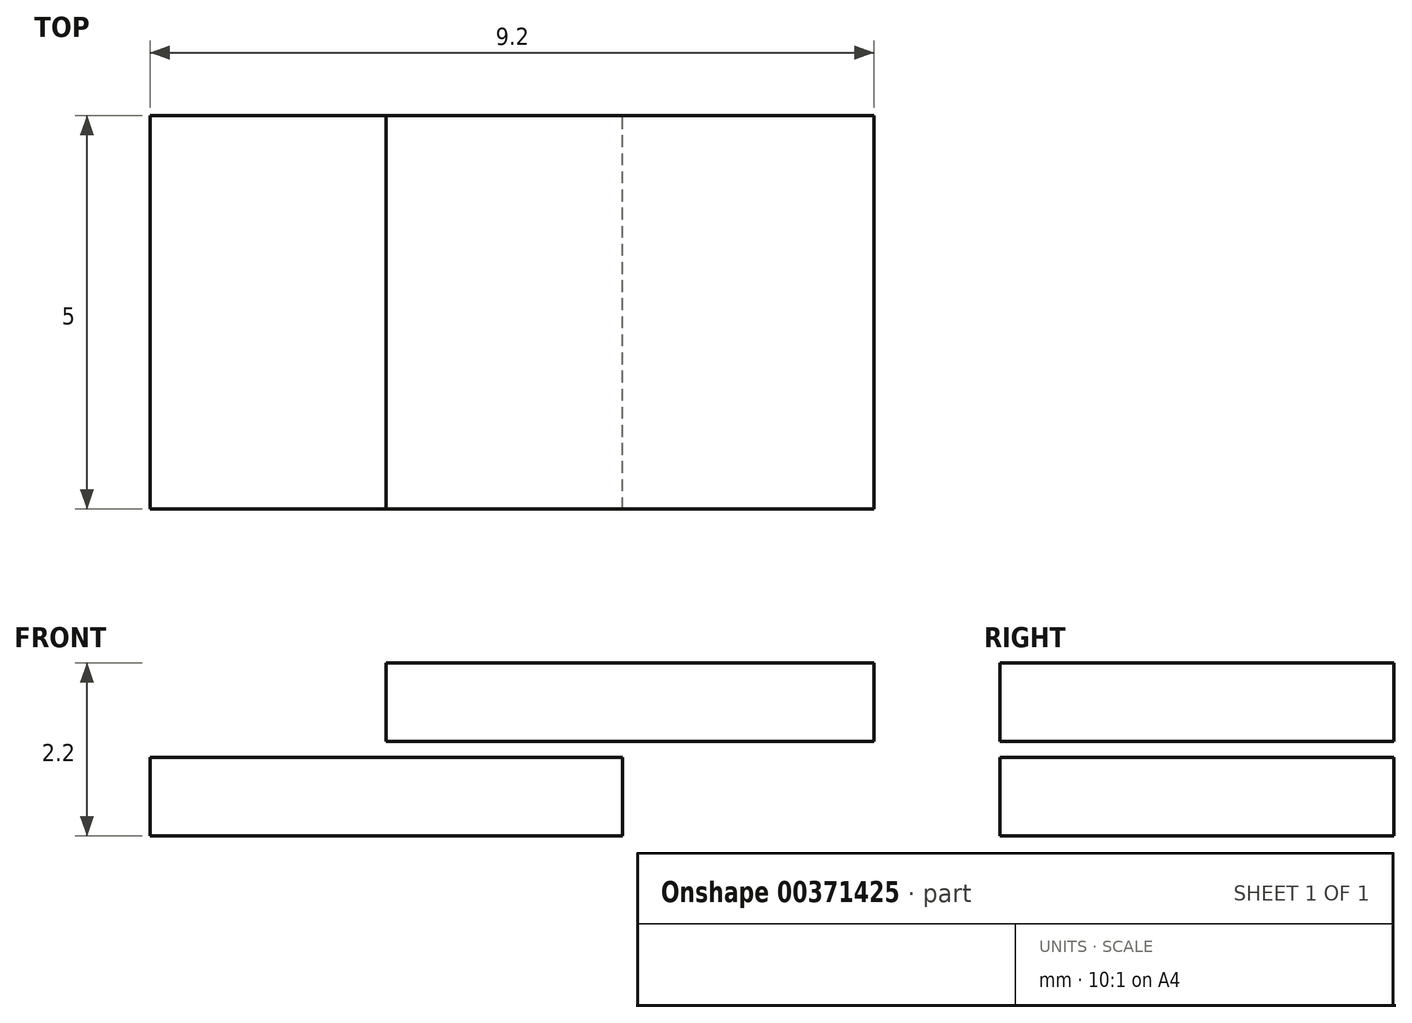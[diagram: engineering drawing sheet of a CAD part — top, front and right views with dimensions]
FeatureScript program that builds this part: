
annotation { "Feature Type Name" : "Feature", "Feature Type Description" : "" }
export const myFeature = defineFeature(function(context is Context, id is Id, definition is map)
    precondition{}
    {
        {
            var Q0;
            Q0=qCreatedBy(makeId("Front.planeOp"),FACE);
            var sketch = newSketch(context, id + "F0", { "sketchPlane" : qUnion([Q0])});
            skLineSegment(sketch, "E0.bottom", {"start": v(0, 0) * mm, "end": v(-6, 0) * mm});
            skLineSegment(sketch, "E0.top", {"start": v(0, 1) * mm, "end": v(-6, 1) * mm});
            skLineSegment(sketch, "E0.left", {"start": v(0, 0) * mm, "end": v(0, 1) * mm});
            skLineSegment(sketch, "E0.right", {"start": v(-6, 0) * mm, "end": v(-6, 1) * mm});
            skLineSegment(sketch, "E1.bottom", {"start": v(-3, 2.2) * mm, "end": v(3.2, 2.2) * mm});
            skLineSegment(sketch, "E1.top", {"start": v(-3, 1.2) * mm, "end": v(3.2, 1.2) * mm});
            skLineSegment(sketch, "E1.left", {"start": v(-3, 2.2) * mm, "end": v(-3, 1.2) * mm});
            skLineSegment(sketch, "E1.right", {"start": v(3.2, 2.2) * mm, "end": v(3.2, 1.2) * mm});
            skLineSegment(sketch, "E2.bottom", {"start": v(3.2, 1.2) * mm, "end": v(0.2, 1.2) * mm});
            skLineSegment(sketch, "E2.top", {"start": v(3.2, 0) * mm, "end": v(0.2, 0) * mm});
            skLineSegment(sketch, "E2.left", {"start": v(3.2, 1.2) * mm, "end": v(3.2, 0) * mm});
            skLineSegment(sketch, "E2.right", {"start": v(0.2, 1.2) * mm, "end": v(0.2, 0) * mm});
            skLineSegment(sketch, "E3.bottom", {"start": v(-6, 1) * mm, "end": v(-3.2, 1) * mm});
            skLineSegment(sketch, "E3.top", {"start": v(-6, 2.2) * mm, "end": v(-3.2, 2.2) * mm});
            skLineSegment(sketch, "E3.left", {"start": v(-6, 1) * mm, "end": v(-6, 2.2) * mm});
            skLineSegment(sketch, "E3.right", {"start": v(-3.2, 1) * mm, "end": v(-3.2, 2.2) * mm});
            skSolve(sketch);
        }
        {
            var Q0;
            Q0=makeQuery(id+"F0.imprint","IMPRINT",FACE,{"disambiguationData":[TD([[makeQuery(id+"F0.imprint","IMPRINT",EDGE,{"derivedFrom":sQuery(id+"F0.wireOp",EDGE,"E0.bottom")}),-1.0]])]});
            var Q1;
            Q1=makeQuery(id+"F0.imprint","IMPRINT",FACE,{"disambiguationData":[TD([[makeQuery(id+"F0.imprint","IMPRINT",EDGE,{"derivedFrom":sQuery(id+"F0.wireOp",EDGE,"E2.bottom")}),1.0]])]});
            var Q2;
            Q2=makeQuery(id+"F0.imprint","IMPRINT",FACE,{"disambiguationData":[TD([[makeQuery(id+"F0.imprint","IMPRINT",EDGE,{"derivedFrom":sQuery(id+"F0.wireOp",EDGE,"E1.bottom")}),-1.0]])]});
            var Q3;
            Q3=makeQuery(id+"F0.imprint","IMPRINT",FACE,{"disambiguationData":[TD([[makeQuery(id+"F0.imprint","IMPRINT",EDGE,{"derivedFrom":sQuery(id+"F0.wireOp",EDGE,"E3.bottom")}),1.0]])]});
            extrude(context, id + "F1", {"entities" : qUnion([Q0, Q1, Q2, Q3]), "depth" : 5 * mm, "offsetDistance" : 25 * mm});
        }
    });
